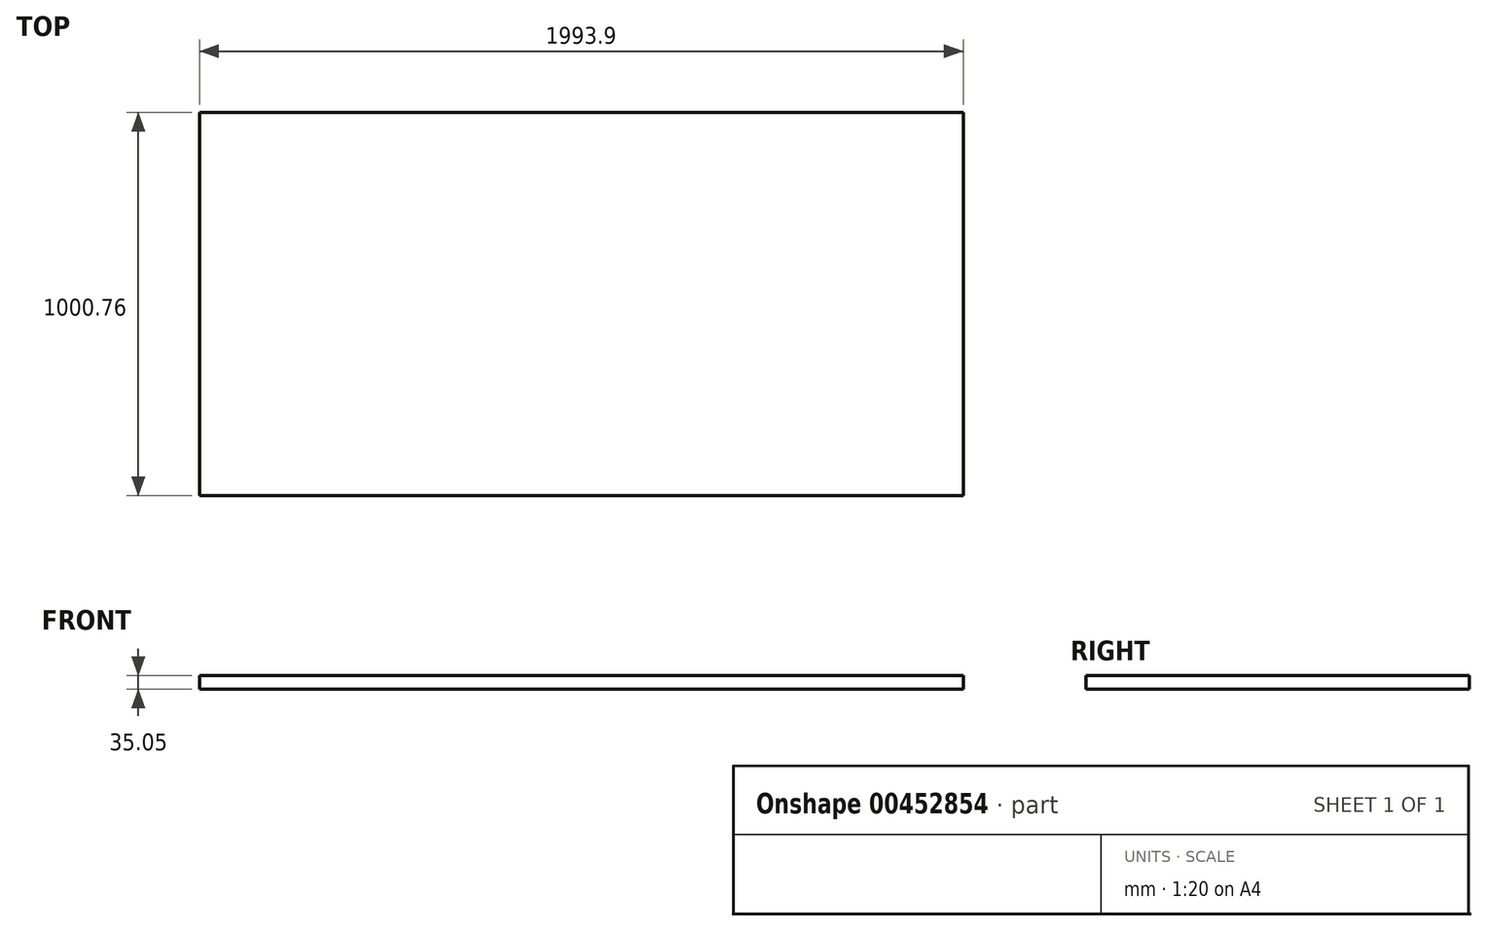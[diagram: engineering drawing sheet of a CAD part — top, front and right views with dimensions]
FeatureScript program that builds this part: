
annotation { "Feature Type Name" : "Feature", "Feature Type Description" : "" }
export const myFeature = defineFeature(function(context is Context, id is Id, definition is map)
    precondition{}
    {
        {
            var Q0;
            Q0=qCreatedBy(makeId("Top.planeOp"),FACE);
            var sketch = newSketch(context, id + "F0", { "sketchPlane" : qUnion([Q0])});
            skLineSegment(sketch, "E0.bottom", {"start": v(-998.35, 193.35) * mm, "end": v(995.55, 193.35) * mm});
            skLineSegment(sketch, "E0.top", {"start": v(-998.35, -807.4) * mm, "end": v(995.55, -807.4) * mm});
            skLineSegment(sketch, "E0.left", {"start": v(-998.35, 193.35) * mm, "end": v(-998.35, -807.4) * mm});
            skLineSegment(sketch, "E0.right", {"start": v(995.55, 193.35) * mm, "end": v(995.55, -807.4) * mm});
            skSolve(sketch);
        }
        {
            var Q0;
            Q0 = qSketchRegion(id + "F0", true);
            extrude(context, id + "F1", {"entities" : qUnion([Q0]), "depth" : 35.05 * mm});
        }
    });
